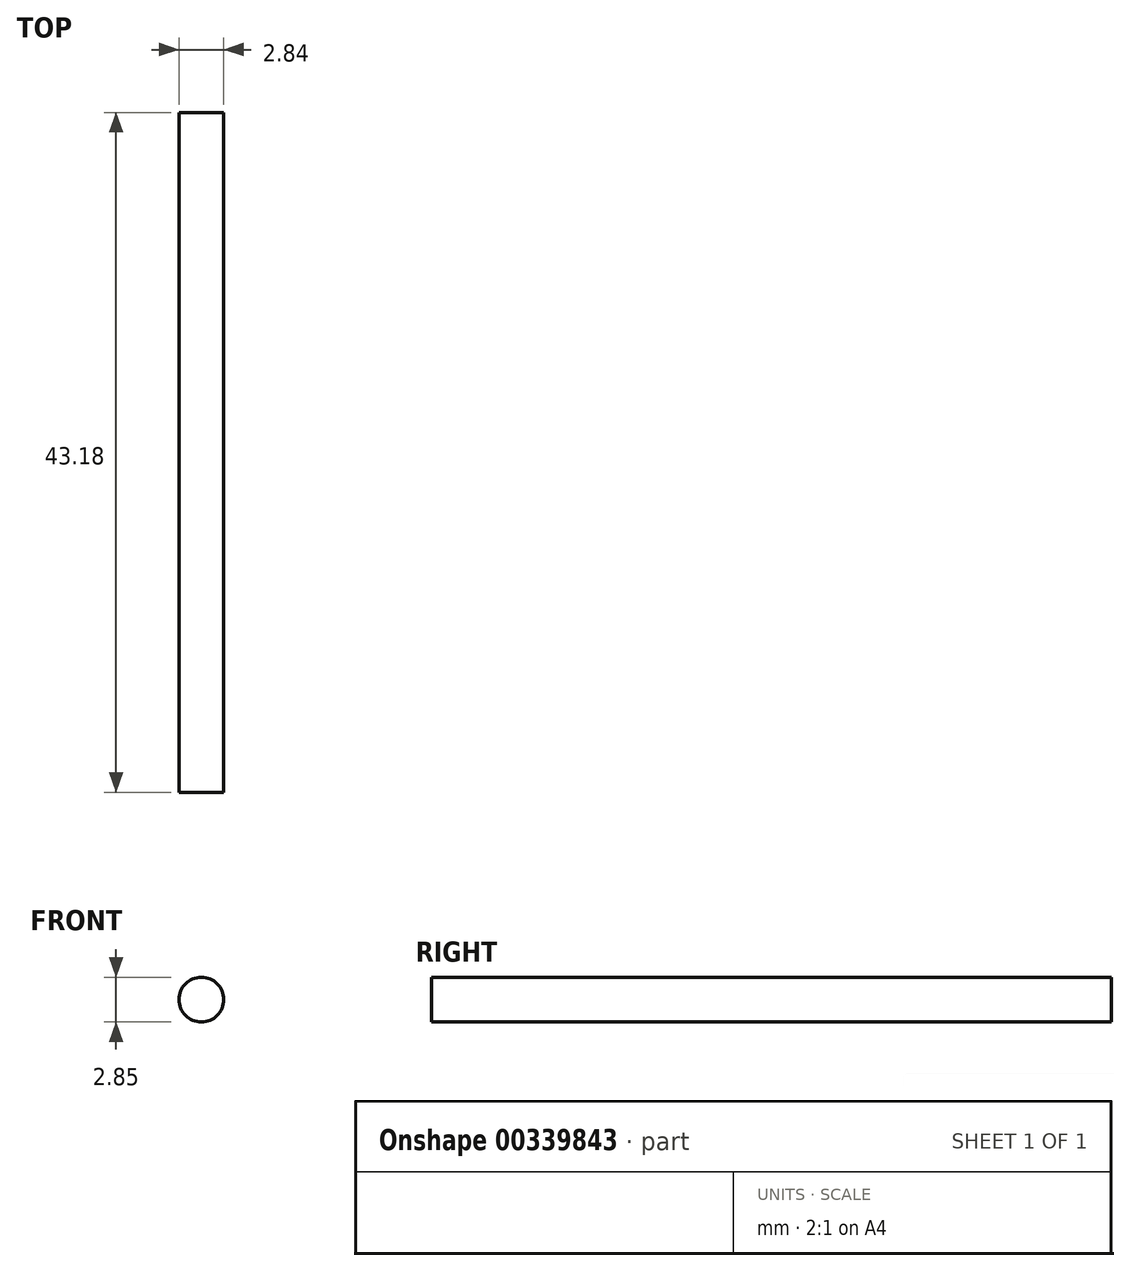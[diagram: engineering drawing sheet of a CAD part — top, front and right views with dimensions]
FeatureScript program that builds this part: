
annotation { "Feature Type Name" : "Feature", "Feature Type Description" : "" }
export const myFeature = defineFeature(function(context is Context, id is Id, definition is map)
    precondition{}
    {
        {
            var Q0;
            Q0=qCreatedBy(makeId("Front.planeOp"),FACE);
            var sketch = newSketch(context, id + "F0", { "sketchPlane" : qUnion([Q0])});
            skCircle(sketch, "E0", {"center": v(-14.38, 10.74) * mm, "radius": 1.42 * mm});
            skSolve(sketch);
        }
        {
            var Q0;
            Q0=makeQuery(id+"F0.imprint","IMPRINT",FACE,{"disambiguationData":[TD([[makeQuery(id+"F0.imprint","IMPRINT",EDGE,{"derivedFrom":sQuery(id+"F0.wireOp",EDGE,"E0")}),1.0]])]});
            extrude(context, id + "F1", {"entities" : qUnion([Q0]), "depth" : 43.18 * mm});
        }
    });
